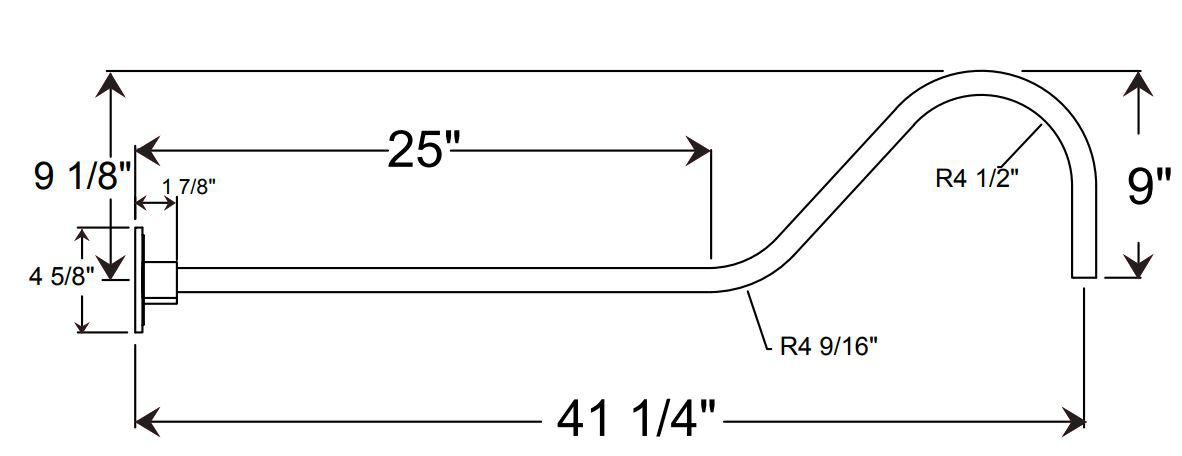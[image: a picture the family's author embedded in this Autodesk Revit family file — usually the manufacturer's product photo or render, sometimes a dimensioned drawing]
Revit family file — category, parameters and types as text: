
# Revit family: Euro Barn EIJ8 (14,16,18,20,22) LED
name_source: partatom
category: Lighting Fixtures
units: mm (PartAtom-declared; Revit-internal decimal feet)

## family parameters
Always vertical = Yes
Cut with Voids When Loaded = No
Light Source = Yes
OmniClass Number = 23.80.70.00
OmniClass Title = Lighting
Part Type = Normal
Room Calculation Point = No
Round Connector Dimension = Use Diameter
Shared = No
Work Plane-Based = No

## types (5) — shared parameters
Apparent Load = 200 VA
Body Colour = Spun aluminium
Body Material = body
CRI = >90
Color Filter = 16777215
Construction Material = Heavy Duty spun aluminum.
Default Elevation = 0' - 0"
Description = 120-277 Voltage
Dimming = 1%
Dimming Lamp Color Temperature Shift = <None>
Efficiency = 65-125 lumens per watt
Fixture Finish = Fixture Finish
Lamp = MB
Life = L70 50,000 hours
Load Classification = Lighting
Manufacturer = ANP Lighting
Mounting Finish = Mounting finish
Photometric Web File = generic.ies
Power Factor = 1
Tilt Angle = 90.00°
URL = https://www.anplighting.com
Voltage = 277 V
Warranty = 5 year limited warranty
Wattage Comments = 200W Max

## per-type parameters (varying)
| type | EU814 | EU816 | EU818 | EU820 | EU822 | Fixture Diameter | Fixture Height | Weight |
| EU814 | Yes | No | No | No | No | 1' - 2" | 0' - 5 1/2" | 3.2 lbs |
| EU816 | No | Yes | No | No | No | 1' - 4" | 0' - 5 1/2" | 3.7 lbs |
| EU818 | No | No | Yes | No | No | 1' - 6" | 0' - 6 1/2" | 4.7 lbs |
| EU820 | No | No | No | Yes | No | 1' - 8" | 0' - 6 1/2" | 5.7 lbs |
| EU822 | No | No | No | No | Yes | 1' - 10" | 0' - 7" | 5.7 lbs |

note: column(s) folded — value = type name in every type: Model

## geometry (parser evidence)
native form markers: Sweep x36
no freeform markers — native parametric forms only
